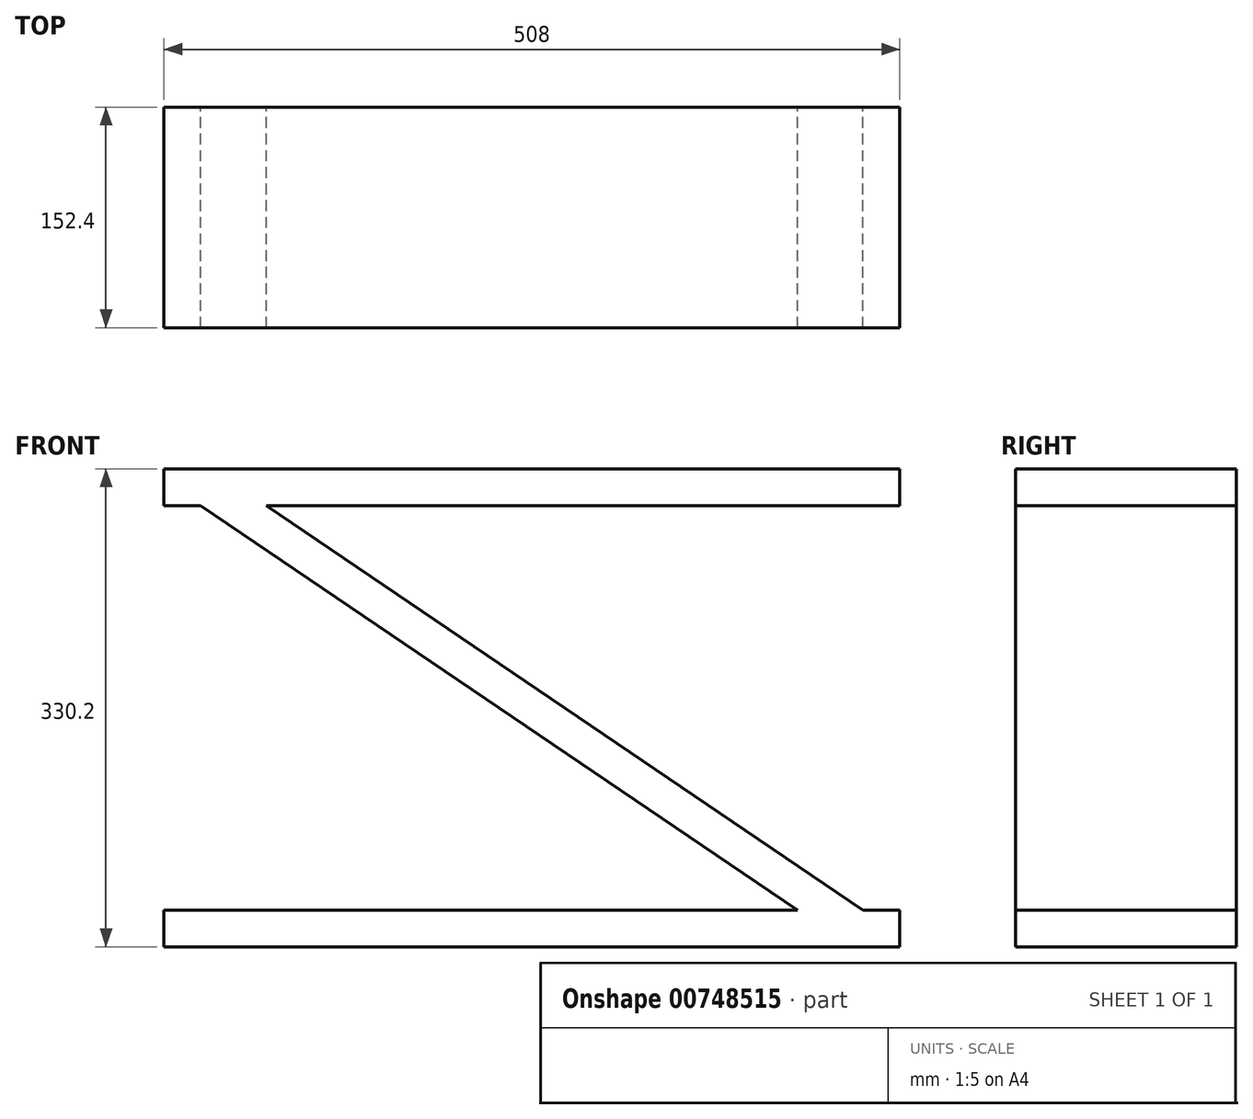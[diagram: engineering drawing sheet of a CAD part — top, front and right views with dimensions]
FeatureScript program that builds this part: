
annotation { "Feature Type Name" : "Feature", "Feature Type Description" : "" }
export const myFeature = defineFeature(function(context is Context, id is Id, definition is map)
    precondition{}
    {
        {
            var Q0;
            Q0=qCreatedBy(makeId("Front.planeOp"),FACE);
            var sketch = newSketch(context, id + "F0", { "sketchPlane" : qUnion([Q0])});
            skLineSegment(sketch, "E0.bottom", {"start": v(-254, -139.7) * mm, "end": v(254, -139.7) * mm, "construction": true});
            skLineSegment(sketch, "E0.top", {"start": v(-254, -165.1) * mm, "end": v(254, -165.1) * mm});
            skLineSegment(sketch, "E0.left", {"start": v(-254, -139.7) * mm, "end": v(-254, -165.1) * mm});
            skLineSegment(sketch, "E0.right", {"start": v(254, -139.7) * mm, "end": v(254, -165.1) * mm});
            skLineSegment(sketch, "E1.bottom", {"start": v(-254, 165.1) * mm, "end": v(254, 165.1) * mm});
            skLineSegment(sketch, "E1.top", {"start": v(-254, 139.7) * mm, "end": v(254, 139.7) * mm, "construction": true});
            skLineSegment(sketch, "E1.left", {"start": v(-254, 165.1) * mm, "end": v(-254, 139.7) * mm});
            skLineSegment(sketch, "E1.right", {"start": v(254, 165.1) * mm, "end": v(254, 139.7) * mm});
            skLineSegment(sketch, "E2", {"start": v(0, 0) * mm, "end": v(0, 139.7) * mm, "construction": true});
            skLineSegment(sketch, "E3", {"start": v(0, 0) * mm, "end": v(0, -139.7) * mm, "construction": true});
            skLineSegment(sketch, "E4", {"start": v(-254, 139.7) * mm, "end": v(-228.6, 139.7) * mm});
            skLineSegment(sketch, "E5", {"start": v(-228.6, 139.7) * mm, "end": v(183.35, -139.7) * mm});
            skLineSegment(sketch, "E6", {"start": v(183.35, -139.7) * mm, "end": v(-254, -139.7) * mm});
            skLineSegment(sketch, "E7", {"start": v(254, 139.7) * mm, "end": v(-183.35, 139.7) * mm});
            skLineSegment(sketch, "E8", {"start": v(-183.35, 139.7) * mm, "end": v(228.6, -139.7) * mm});
            skLineSegment(sketch, "E9", {"start": v(228.6, -139.7) * mm, "end": v(254, -139.7) * mm});
            skSolve(sketch);
        }
        {
            var Q0;
            Q0 = qSketchRegion(id + "F0", true);
            extrude(context, id + "F1", {"entities" : qUnion([Q0]), "depth" : 152.4 * mm, "offsetDistance" : 25.4 * mm});
        }
    });
